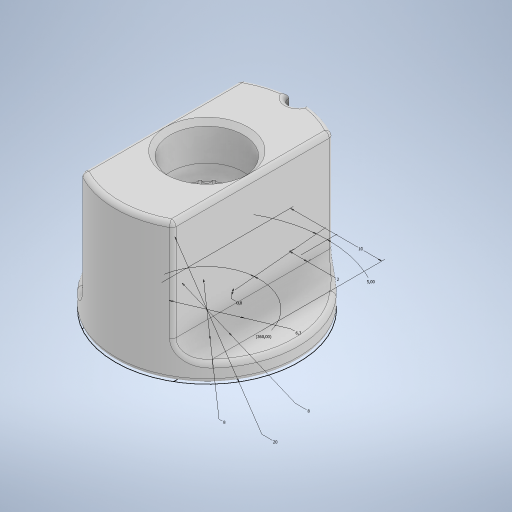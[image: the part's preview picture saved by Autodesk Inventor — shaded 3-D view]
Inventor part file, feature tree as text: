
AUTODESK INVENTOR PART (.ipt)
format: ipt  version: 2024 (Build 280153000, 153)  size: 613,376 bytes
history: native  units: mm
features: extrude x7, fillet x7, sketch x3, other x1, revolve x1, chamfer x1, projected_geometry x1
ambient origin geometry x8: Origin, YZ Plane, XZ Plane, XY Plane, X Axis, Y Axis, Z Axis, Center Point
bodies: Body1 (feature_tree)
feature tree (21):
  other  "Твердое тело1"
  sketch  "Эскиз1"
  extrude  "Выдавливание1"  Depth=6.15mm
  extrude  "Выдавливание2"  Depth=8.0mm
  extrude  "Выдавливание3"  Depth=0.8mm
  extrude  "Выдавливание4"  Depth=180.0mm TaperAngle=360.0deg
  extrude  "Выдавливание5"  Depth=20.0mm
  fillet  "Сопряжение2"  Radius=10.0mm
  revolve  "Вращение1"
  fillet  "Сопряжение3"  Radius=8.0mm
  chamfer  "Фаска1"  Distance=2.0mm
  fillet  "Сопряжение7"  Radius=2.0mm
  fillet  "Сопряжение8"  Radius=15.0mm
  extrude  "Выдавливание7"  Depth=4.0mm TaperAngle=0.0deg
  fillet  "Сопряжение11"  [1 undecoded]
  extrude  "Выдавливание8"  Depth=5.0mm TaperAngle=0.0deg
  fillet  "Сопряжение12"  Radius=1.0mm
  fillet  "Сопряжение13"  [1 undecoded]
  sketch  "Эскиз2"
  projected_geometry  "Спроецированная петля1"
  sketch  "Эскиз4"
note: 2 required parameter values undecoded (feature->parameter linkage not recoverable at this tier; creation-order binding heuristic only, values carry confidence <= 0.55)
